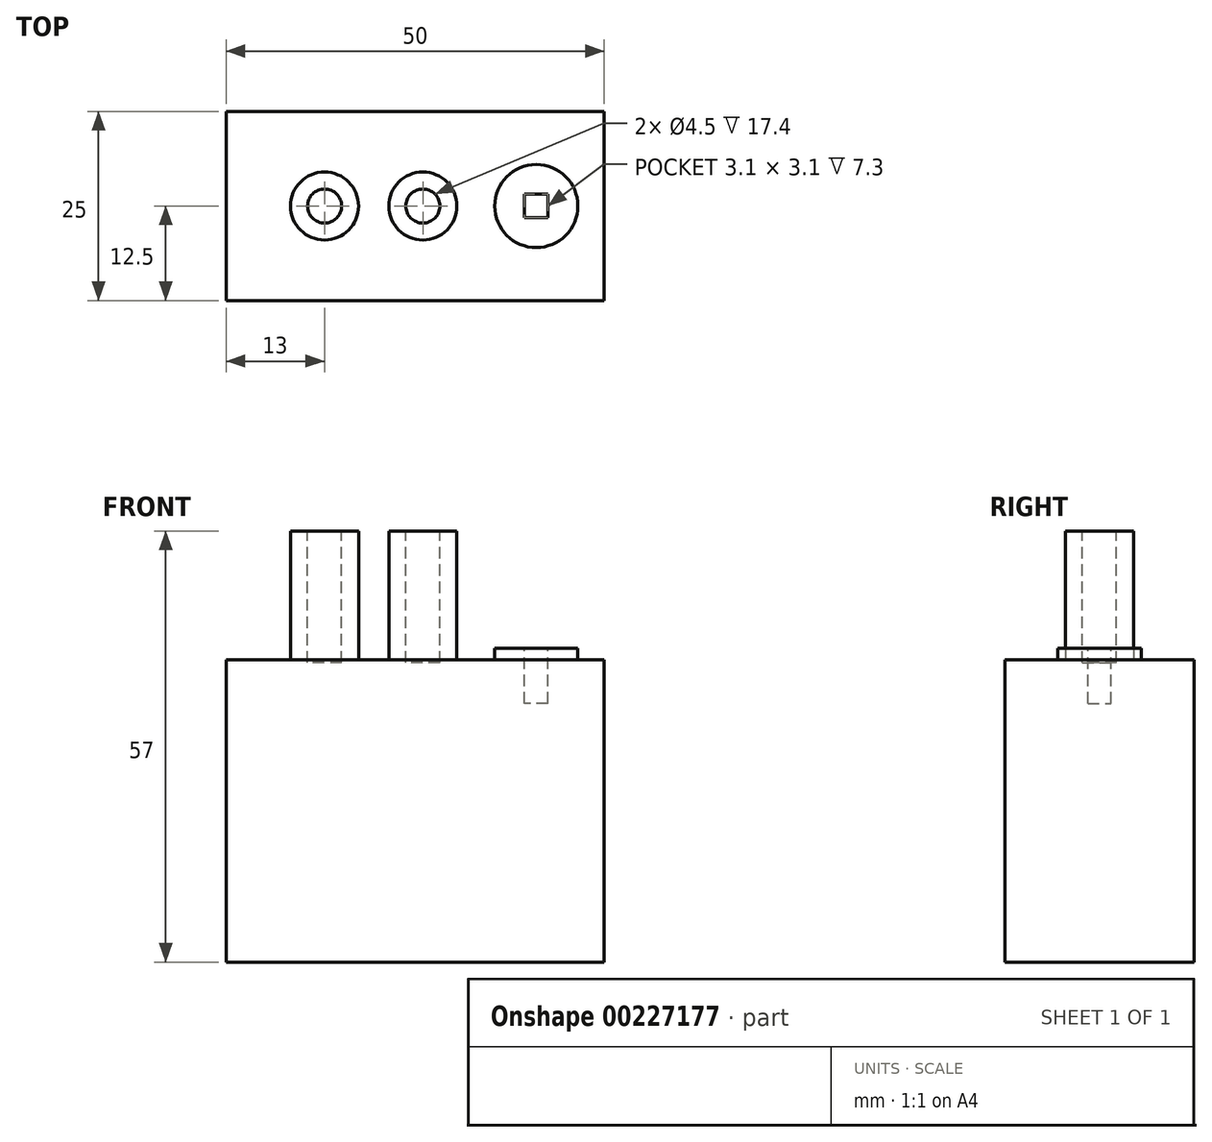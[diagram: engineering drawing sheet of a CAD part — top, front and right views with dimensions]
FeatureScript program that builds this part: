
annotation { "Feature Type Name" : "Feature", "Feature Type Description" : "" }
export const myFeature = defineFeature(function(context is Context, id is Id, definition is map)
    precondition{}
    {
        {
            var Q0;
            Q0=qCreatedBy(makeId("Top.planeOp"),FACE);
            var sketch = newSketch(context, id + "F0", { "sketchPlane" : qUnion([Q0])});
            skLineSegment(sketch, "E0.bottom", {"start": v(25, -12.5) * mm, "end": v(-25, -12.5) * mm});
            skLineSegment(sketch, "E0.top", {"start": v(25, 12.5) * mm, "end": v(-25, 12.5) * mm});
            skLineSegment(sketch, "E0.left", {"start": v(25, -12.5) * mm, "end": v(25, 12.5) * mm});
            skLineSegment(sketch, "E0.right", {"start": v(-25, -12.5) * mm, "end": v(-25, 12.5) * mm});
            skPoint(sketch, "E0.middle", {"position": v(0, 0) * mm});
            skSolve(sketch);
        }
        {
            var Q0;
            Q0 = qSketchRegion(id + "F0", true);
            extrude(context, id + "F1", {"entities" : qUnion([Q0]), "endBound" : BoundingType.SYMMETRIC, "depth" : 40 * mm});
        }
        {
            var Q0;
            Q0=makeQuery(id+"F1.opExtrude","CAP_FACE",FACE,{"disambiguationData":[OSD([sQuery(id+"F0.wireOp",EDGE,"E0.bottom"),sQuery(id+"F0.wireOp",EDGE,"E0.top"),sQuery(id+"F0.wireOp",EDGE,"E0.left"),sQuery(id+"F0.wireOp",EDGE,"E0.right")])],"isStart":false});
            var sketch = newSketch(context, id + "F2", { "sketchPlane" : qUnion([Q0])});
            skCircle(sketch, "E1", {"center": v(-12, 0) * mm, "radius": 4.5 * mm});
            skCircle(sketch, "E2.1.0.0", {"center": v(1, 0) * mm, "radius": 4.5 * mm});
            skLineSegment(sketch, "E2.direction1", {"start": v(-12, 0) * mm, "end": v(1, 0) * mm, "construction": true});
            skCircle(sketch, "E3", {"center": v(16, 0) * mm, "radius": 5.5 * mm});
            skSolve(sketch);
        }
        {
            var Q0;
            Q0=makeQuery(id+"F2.imprint","IMPRINT",FACE,{"disambiguationData":[TD([[makeQuery(id+"F2.imprint","IMPRINT",EDGE,{"derivedFrom":sQuery(id+"F2.wireOp",EDGE,"E3")}),1.0]])]});
            extrude(context, id + "F3", {"entities" : qUnion([Q0]), "operationType" : NewBodyOperationType.ADD, "depth" : 1.5 * mm});
        }
        {
            var Q0;
            Q0=makeQuery(id+"F2.imprint","IMPRINT",FACE,{"disambiguationData":[TD([[makeQuery(id+"F2.imprint","IMPRINT",EDGE,{"derivedFrom":sQuery(id+"F2.wireOp",EDGE,"E1")}),1.0]])]});
            var Q1;
            Q1=makeQuery(id+"F2.imprint","IMPRINT",FACE,{"disambiguationData":[TD([[makeQuery(id+"F2.imprint","IMPRINT",EDGE,{"derivedFrom":sQuery(id+"F2.wireOp",EDGE,"E2.1.0.0")}),1.0]])]});
            extrude(context, id + "F4", {"entities" : qUnion([Q0, Q1]), "operationType" : NewBodyOperationType.ADD, "depth" : 17 * mm});
        }
        {
            var Q0;
            Q0=makeQuery(id+"F3.opExtrude","CAP_FACE",FACE,{"disambiguationData":[OSD([sQuery(id+"F2.wireOp",EDGE,"E3")])],"isStart":false});
            var sketch = newSketch(context, id + "F5", { "sketchPlane" : qUnion([Q0])});
            skLineSegment(sketch, "E4.bottom", {"start": v(17.55, -1.55) * mm, "end": v(14.45, -1.55) * mm});
            skLineSegment(sketch, "E4.top", {"start": v(17.55, 1.55) * mm, "end": v(14.45, 1.55) * mm});
            skLineSegment(sketch, "E4.left", {"start": v(17.55, -1.55) * mm, "end": v(17.55, 1.55) * mm});
            skLineSegment(sketch, "E4.right", {"start": v(14.45, -1.55) * mm, "end": v(14.45, 1.55) * mm});
            skPoint(sketch, "E4.middle", {"position": v(16, 0) * mm});
            skSolve(sketch);
        }
        {
            var Q0;
            Q0 = qSketchRegion(id + "F5", true);
            extrude(context, id + "F6", {"entities" : qUnion([Q0]), "operationType" : NewBodyOperationType.REMOVE, "oppositeDirection" : true, "depth" : 7.3 * mm});
        }
        {
            var Q0;
            Q0=makeQuery(id+"F4.opExtrude","CAP_FACE",FACE,{"disambiguationData":[OSD([sQuery(id+"F2.wireOp",EDGE,"E1")])],"isStart":false});
            var sketch = newSketch(context, id + "F7", { "sketchPlane" : qUnion([Q0])});
            skCircle(sketch, "E5", {"center": v(-12, 0) * mm, "radius": 2.25 * mm});
            skCircle(sketch, "E6.1.0.0", {"center": v(1, 0) * mm, "radius": 2.25 * mm});
            skLineSegment(sketch, "E6.direction1", {"start": v(-12, 0) * mm, "end": v(1, 0) * mm, "construction": true});
            skSolve(sketch);
        }
        {
            var Q0;
            Q0=makeQuery(id+"F7.imprint","IMPRINT",FACE,{"disambiguationData":[TD([[makeQuery(id+"F7.imprint","IMPRINT",EDGE,{"derivedFrom":sQuery(id+"F7.wireOp",EDGE,"E5")}),1.0]])]});
            var Q1;
            Q1=makeQuery(id+"F7.imprint","IMPRINT",FACE,{"disambiguationData":[TD([[makeQuery(id+"F7.imprint","IMPRINT",EDGE,{"derivedFrom":sQuery(id+"F7.wireOp",EDGE,"E6.1.0.0")}),1.0]])]});
            var Q2;
            Q2=sQuery(id+"F7.wireOp",EDGE,"E5");
            var Q3;
            Q3=sQuery(id+"F7.wireOp",EDGE,"E6.1.0.0");
            extrude(context, id + "F8", {"entities" : qUnion([Q0, Q1]), "operationType" : NewBodyOperationType.REMOVE, "surfaceEntities" : qUnion([Q2, Q3]), "oppositeDirection" : true, "depth" : 17.4 * mm});
        }
    });
